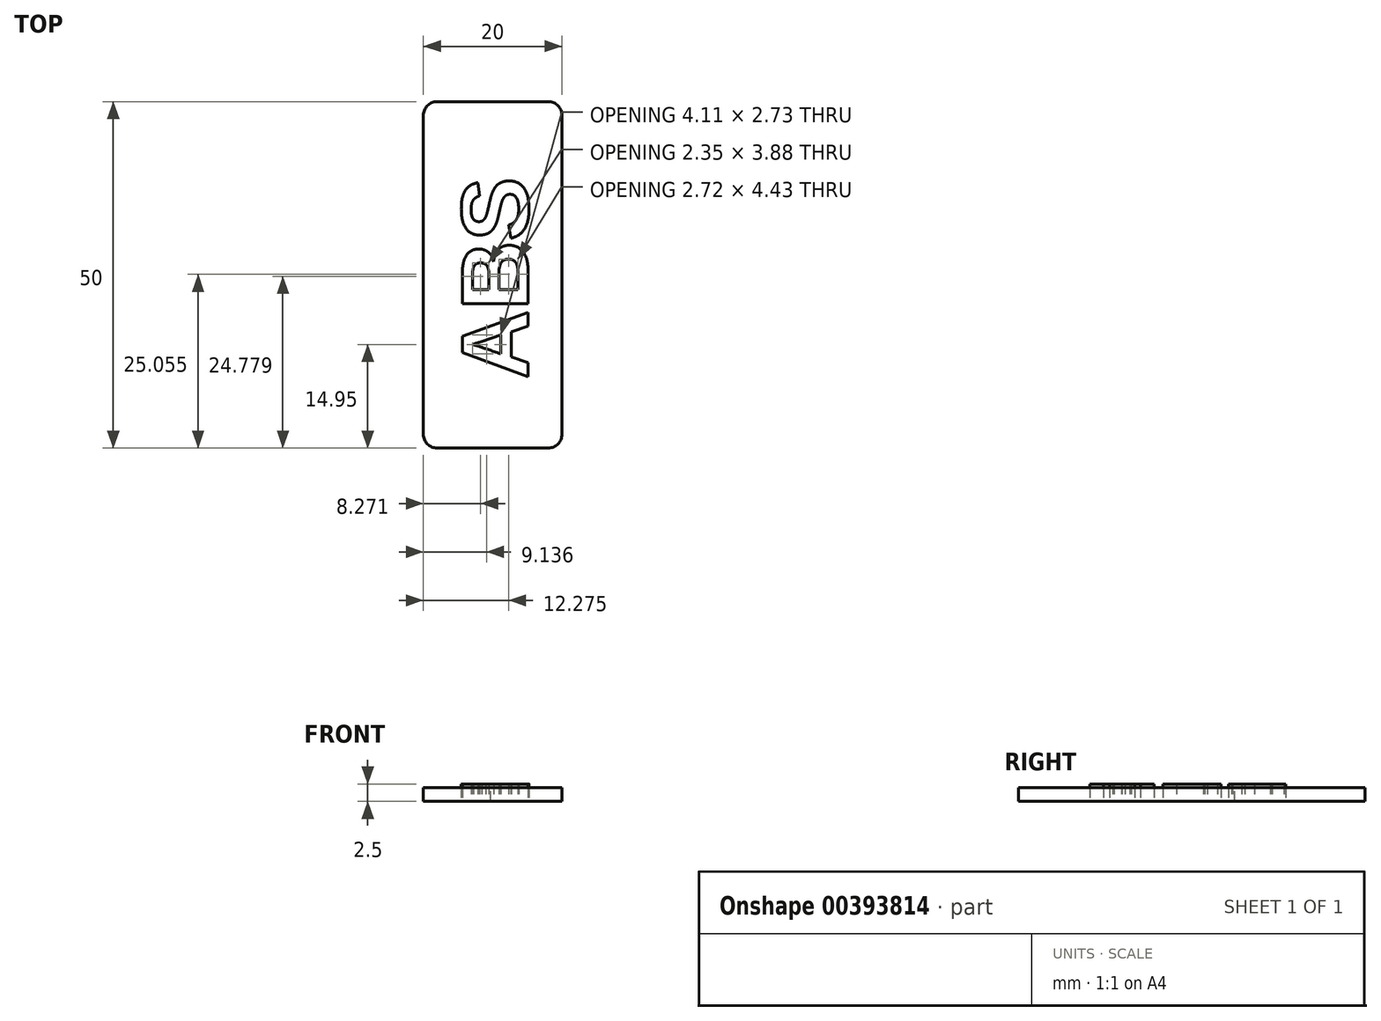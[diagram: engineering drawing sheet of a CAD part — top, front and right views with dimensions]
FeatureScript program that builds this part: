
annotation { "Feature Type Name" : "Feature", "Feature Type Description" : "" }
export const myFeature = defineFeature(function(context is Context, id is Id, definition is map)
    precondition{}
    {
        {
            var Q0;
            Q0=qCreatedBy(makeId("Top.planeOp"),FACE);
            var sketch = newSketch(context, id + "F0", { "sketchPlane" : qUnion([Q0])});
            skLineSegment(sketch, "E0.bottom", {"start": v(-20, -25) * mm, "end": v(0, -25) * mm});
            skLineSegment(sketch, "E0.top", {"start": v(-20, 25) * mm, "end": v(0, 25) * mm});
            skLineSegment(sketch, "E0.left", {"start": v(-20, -25) * mm, "end": v(-20, 25) * mm});
            skLineSegment(sketch, "E0.right", {"start": v(0, -25) * mm, "end": v(0, 25) * mm});
            skSolve(sketch);
        }
        {
            var Q0;
            Q0=makeQuery(id+"F0.imprint","IMPRINT",FACE,{"disambiguationData":[TD([[makeQuery(id+"F0.imprint","IMPRINT",EDGE,{"derivedFrom":sQuery(id+"F0.wireOp",EDGE,"E0.bottom")}),1.0]])]});
            extrude(context, id + "F1", {"entities" : qUnion([Q0]), "depth" : 2 * mm});
        }
        {
            var Q0;
            Q0=makeQuery(id+"F1.opExtrude","SWEPT_EDGE",EDGE,{"disambiguationData":[OSD([sQuery(id+"F0.wireOp",EDGE,"E0.bottom"),sQuery(id+"F0.wireOp",EDGE,"E0.right")])]});
            var Q1;
            Q1=makeQuery(id+"F1.opExtrude","SWEPT_EDGE",EDGE,{"disambiguationData":[OSD([sQuery(id+"F0.wireOp",EDGE,"E0.bottom"),sQuery(id+"F0.wireOp",EDGE,"E0.left")])]});
            var Q2;
            Q2=makeQuery(id+"F1.opExtrude","SWEPT_EDGE",EDGE,{"disambiguationData":[OSD([sQuery(id+"F0.wireOp",EDGE,"E0.top"),sQuery(id+"F0.wireOp",EDGE,"E0.right")])]});
            var Q3;
            Q3=makeQuery(id+"F1.opExtrude","SWEPT_EDGE",EDGE,{"disambiguationData":[OSD([sQuery(id+"F0.wireOp",EDGE,"E0.top"),sQuery(id+"F0.wireOp",EDGE,"E0.left")])]});
            fillet(context, id + "F2", {"entities" : qUnion([Q0, Q1, Q2, Q3]), "radius" : 2 * mm, "tangentPropagation" : true, "allowEdgeOverflow" : false});
        }
        {
            var Q0;
            Q0=qCreatedBy(makeId("Top.planeOp"),FACE);
            var sketch = newSketch(context, id + "F3", { "sketchPlane" : qUnion([Q0])});
            skText(sketch, "E1", { "text": "ABS", "fontName": "Arimo-Bold.ttf"});
            const initialGuessF3  = {"E1": [-0.00489, -0.01503, 0, 1, 0.00993]};
            skSetInitialGuess(sketch, initialGuessF3);
            skSolve(sketch);
        }
        {
            var Q0;
            Q0 = qSketchRegion(id + "F3", true);
            extrude(context, id + "F4", {"entities" : qUnion([Q0]), "depth" : 2.5 * mm});
        }
    });
